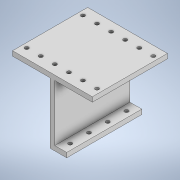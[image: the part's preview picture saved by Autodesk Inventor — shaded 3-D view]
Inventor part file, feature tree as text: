
AUTODESK INVENTOR PART (.ipt)
format: ipt  version: 2022.1 (Build 261234020, 234B)  size: 164,864 bytes
history: native  units: in
note: dims shown in document units (in); Inventor stores cm internally (conversion verified against a paired STEP export)
features: sketch x5, extrude x3, hole x2
ambient origin geometry x8: Origin, YZ Plane, XZ Plane, XY Plane, X Axis, Y Axis, Z Axis, Center Point
bodies: Solid1 (feature_tree)
feature tree (10):
  extrude  "Extrusion1"  Depth=0.8862in
  extrude  "Extrusion2"  TaperAngle=0.0deg  [1 undecoded]
  extrude  "Extrusion3"  Depth=3.0in
  hole  "Hole1"  [1 undecoded]
  hole  "Hole2"  [1 undecoded]
  sketch  "Sketch1"  dims[d0=4.0in d1=0.8862in]
  sketch  "Sketch2"  dims[d2=0.25in d3=0.0in]
  sketch  "Sketch3"  dims[d4=0.25in d5=3.0in]
  sketch  "Sketch4"  dims[d6=0.0in d7=2.0in]
  sketch  "Sketch5"  dims[d8=2.0in d9=0.25in d10=0.0in d11=0.5in d12=1.5748in d14=1.0in d15=0.3937in d17=1.0in d19=0.201in d20=0.75in d21=0.563in d22=0.12in d23=0.5635in d24=0.281in d25=0.0in d26=1.5in d27=3.0in d28=0.25in d29=0.7874in d31=3.0in d32=2.7559in d34=0.75in d37=0.201in d38=0.75in d39=0.375in d40=0.25in d41=0.5635in d42=1.0in d43=0.0in]
note: 3 required parameter values undecoded (feature->parameter linkage not recoverable at this tier; creation-order binding heuristic only, values carry confidence <= 0.55)
